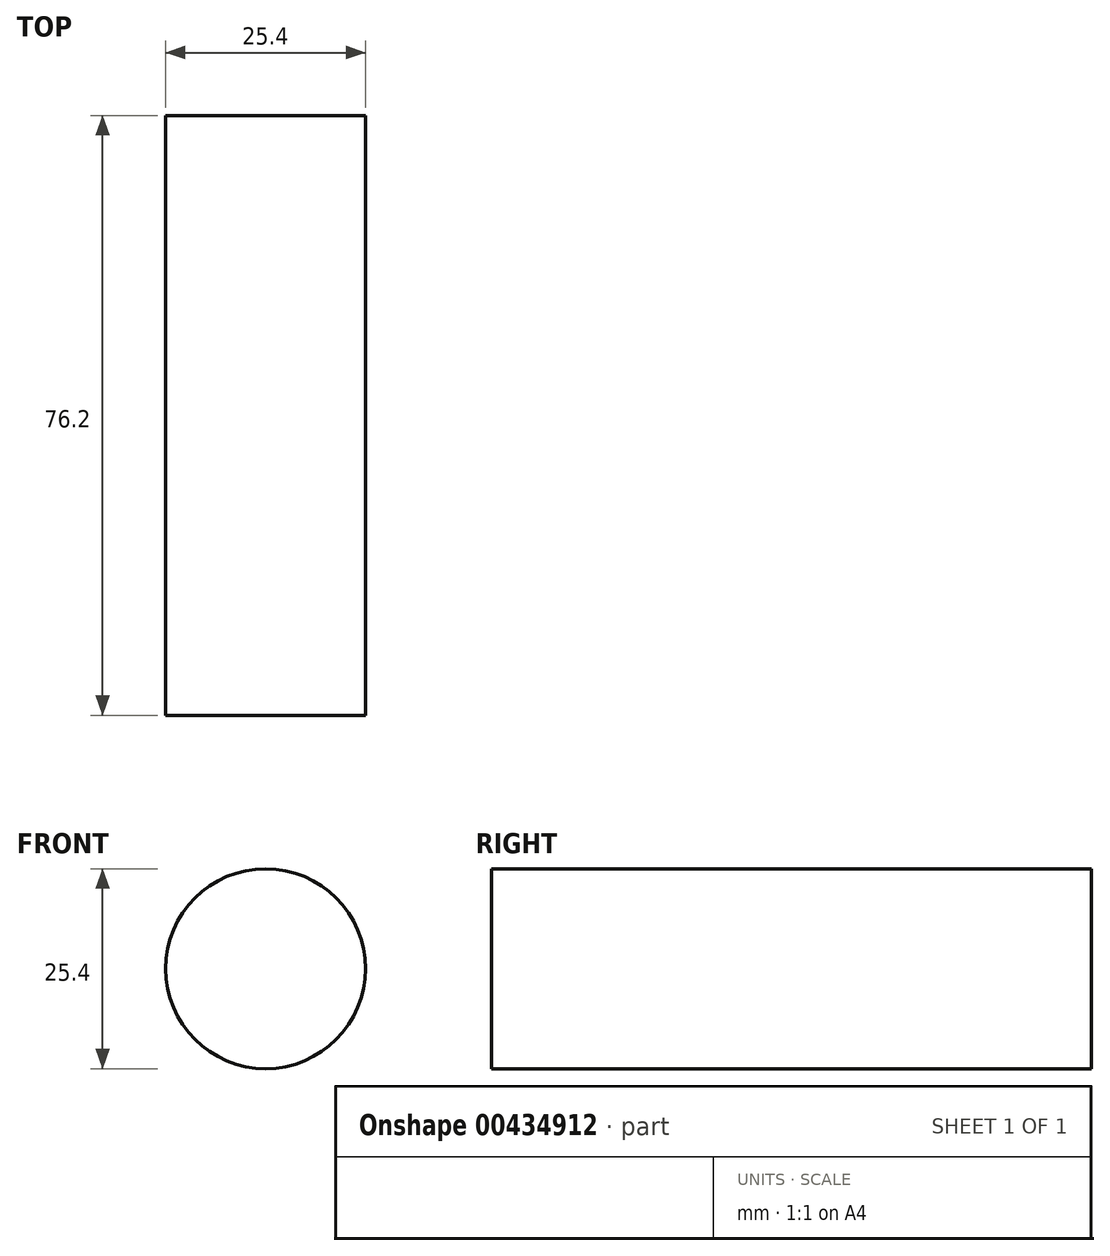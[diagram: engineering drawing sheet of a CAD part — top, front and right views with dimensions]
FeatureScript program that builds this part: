
annotation { "Feature Type Name" : "Feature", "Feature Type Description" : "" }
export const myFeature = defineFeature(function(context is Context, id is Id, definition is map)
    precondition{}
    {
        {
            var Q0;
            Q0=qCreatedBy(makeId("Front.planeOp"),FACE);
            var sketch = newSketch(context, id + "F0", { "sketchPlane" : qUnion([Q0])});
            skCircle(sketch, "E0", {"center": v(-25.67, 30.37) * mm, "radius": 12.7 * mm});
            skSolve(sketch);
        }
        {
            var Q0;
            Q0 = qSketchRegion(id + "F0", true);
            extrude(context, id + "F1", {"entities" : qUnion([Q0]), "depth" : 76.2 * mm});
        }
    });
